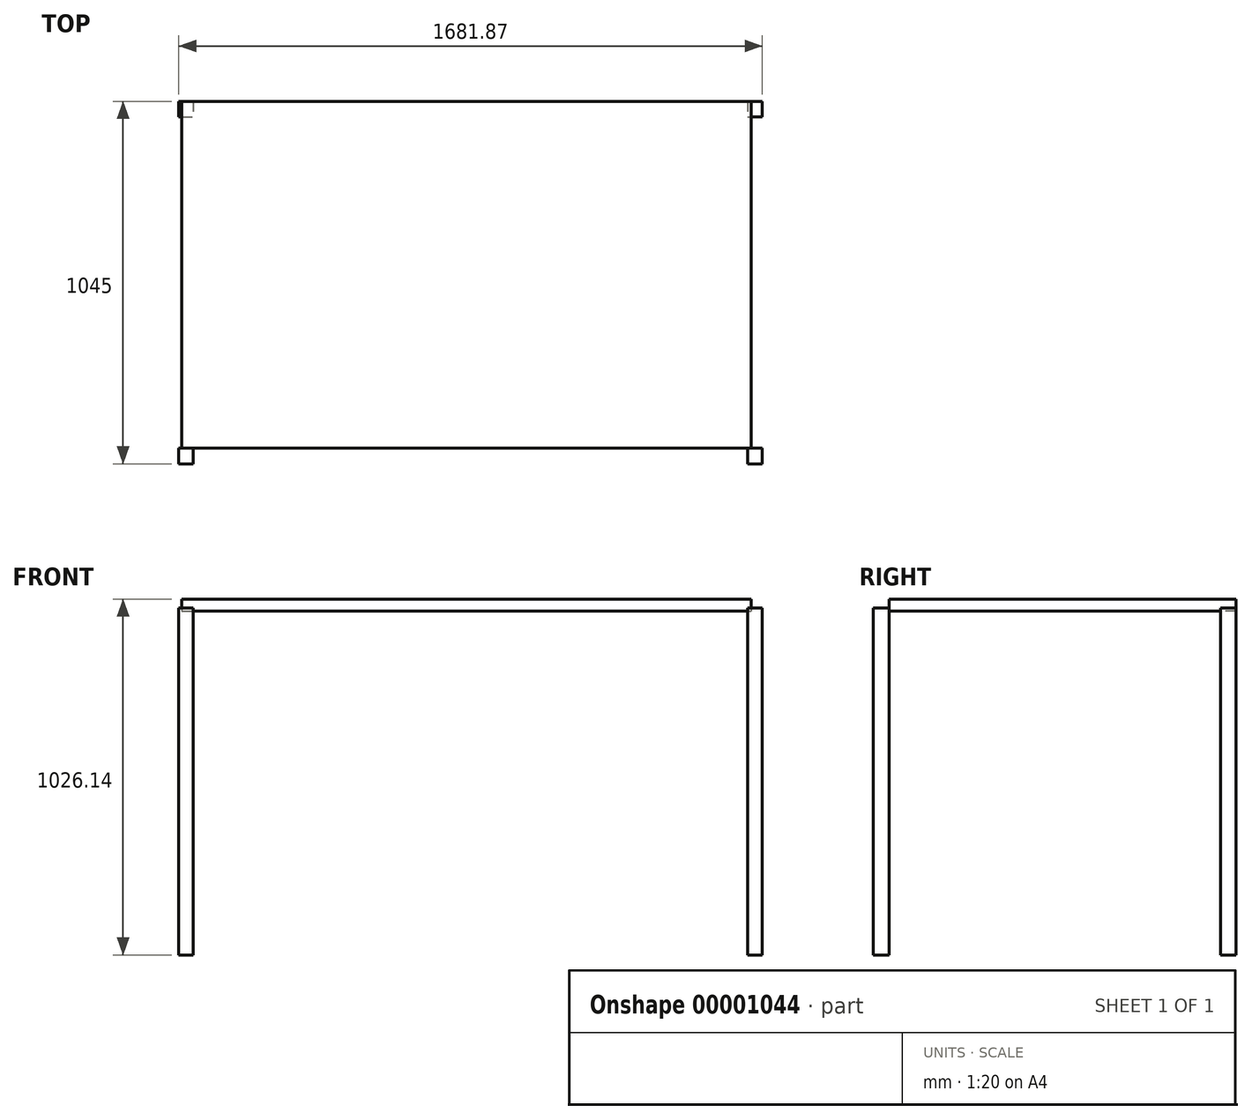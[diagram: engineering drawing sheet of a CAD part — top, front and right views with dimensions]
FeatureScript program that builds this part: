
annotation { "Feature Type Name" : "Feature", "Feature Type Description" : "" }
export const myFeature = defineFeature(function(context is Context, id is Id, definition is map)
    precondition{}
    {
        {
            var Q0;
            Q0=qCreatedBy(makeId("Top.planeOp"),FACE);
            var sketch = newSketch(context, id + "F0", { "sketchPlane" : qUnion([Q0])});
            skLineSegment(sketch, "E0.bottom", {"start": v(-55.77, 808.91) * mm, "end": v(1584.23, 808.91) * mm});
            skLineSegment(sketch, "E0.top", {"start": v(-55.77, -191.09) * mm, "end": v(1584.23, -191.09) * mm});
            skLineSegment(sketch, "E0.left", {"start": v(-55.77, 808.91) * mm, "end": v(-55.77, -191.09) * mm});
            skLineSegment(sketch, "E0.right", {"start": v(1584.23, 808.91) * mm, "end": v(1584.23, -191.09) * mm});
            skSolve(sketch);
        }
        {
            var Q0;
            Q0=qCreatedBy(makeId("Top.planeOp"),FACE);
            var sketch = newSketch(context, id + "F1", { "sketchPlane" : qUnion([Q0])});
            skLineSegment(sketch, "E1.bottom", {"start": v(-344.59, -179) * mm, "end": v(-302.72, -179) * mm});
            skLineSegment(sketch, "E1.top", {"start": v(-344.59, -224) * mm, "end": v(-302.72, -224) * mm});
            skLineSegment(sketch, "E1.left", {"start": v(-344.59, -179) * mm, "end": v(-344.59, -224) * mm});
            skLineSegment(sketch, "E1.right", {"start": v(-302.72, -179) * mm, "end": v(-302.72, -224) * mm});
            skSolve(sketch);
        }
        {
            var Q0;
            Q0=makeQuery(id+"F0.imprint","IMPRINT",FACE,{"disambiguationData":[TD([[makeQuery(id+"F0.imprint","IMPRINT",EDGE,{"derivedFrom":sQuery(id+"F0.wireOp",EDGE,"E0.bottom")}),-1.0]])]});
            extrude(context, id + "F2", {"entities" : qUnion([Q0]), "depth" : 35 * mm});
        }
        {
            var Q0;
            Q0 = qSketchRegion(id + "F1", true);
            extrude(context, id + "F3", {"entities" : qUnion([Q0]), "depth" : 1000 * mm});
        }
        {
            var Q0;
            Q0=makeQuery(id+"F3.opExtrude","SWEPT_BODY",BODY,{"disambiguationData":[OSD([sQuery(id+"F1.wireOp",EDGE,"E1.bottom"),sQuery(id+"F1.wireOp",EDGE,"E1.top"),sQuery(id+"F1.wireOp",EDGE,"E1.left"),sQuery(id+"F1.wireOp",EDGE,"E1.right")])]});
            transform(context, id + "F4", {"entities" : qUnion([Q0]), "transformType" : TransformType.TRANSLATION_3D, "dx" : 0 * mm, "dy" : 1000 * mm, "dz" : 0 * mm, "makeCopy" : true});
        }
        {
            var Q0;
            Q0=makeQuery(id+"F3.opExtrude","SWEPT_BODY",BODY,{"disambiguationData":[OSD([sQuery(id+"F1.wireOp",EDGE,"E1.bottom"),sQuery(id+"F1.wireOp",EDGE,"E1.top"),sQuery(id+"F1.wireOp",EDGE,"E1.left"),sQuery(id+"F1.wireOp",EDGE,"E1.right")])]});
            transform(context, id + "F5", {"entities" : qUnion([Q0]), "transformType" : TransformType.TRANSLATION_3D, "dx" : 1640 * mm, "dy" : 0 * mm, "dz" : 0 * mm, "makeCopy" : true});
        }
        {
            var Q0;
            Q0=makeQuery(id+"F4.opPattern","COPY",BODY,{"derivedFrom":makeQuery(id+"F3.opExtrude","SWEPT_BODY",BODY,{"disambiguationData":[OSD([sQuery(id+"F1.wireOp",EDGE,"E1.bottom"),sQuery(id+"F1.wireOp",EDGE,"E1.top"),sQuery(id+"F1.wireOp",EDGE,"E1.left"),sQuery(id+"F1.wireOp",EDGE,"E1.right")])]}),"instanceName":"1"});
            transform(context, id + "F6", {"entities" : qUnion([Q0]), "transformType" : TransformType.TRANSLATION_3D, "dx" : 1640 * mm, "dy" : 0 * mm, "dz" : 0 * mm, "makeCopy" : true});
        }
        {
            var Q0;
            Q0=makeQuery(id+"F2.opExtrude","SWEPT_BODY",BODY,{"disambiguationData":[OSD([sQuery(id+"F0.wireOp",EDGE,"E0.bottom"),sQuery(id+"F0.wireOp",EDGE,"E0.top"),sQuery(id+"F0.wireOp",EDGE,"E0.left"),sQuery(id+"F0.wireOp",EDGE,"E0.right")])]});
            transform(context, id + "F7", {"entities" : qUnion([Q0]), "transformType" : TransformType.TRANSLATION_3D, "dx" : -279.8 * mm, "dy" : 40.27 * mm, "dz" : 1012.18 * mm, "makeCopy" : false});
        }
        {
            var Q0;
            Q0=makeQuery(id+"F2.opExtrude","SWEPT_BODY",BODY,{"disambiguationData":[OSD([sQuery(id+"F0.wireOp",EDGE,"E0.bottom"),sQuery(id+"F0.wireOp",EDGE,"E0.top"),sQuery(id+"F0.wireOp",EDGE,"E0.left"),sQuery(id+"F0.wireOp",EDGE,"E0.right")])]});
            transform(context, id + "F8", {"entities" : qUnion([Q0]), "transformType" : TransformType.TRANSLATION_3D, "dx" : 0 * mm, "dy" : 0 * mm, "dz" : -21.05 * mm, "makeCopy" : false});
        }
        {
            var Q0;
            Q0=makeQuery(id+"F2.opExtrude","SWEPT_BODY",BODY,{"disambiguationData":[OSD([sQuery(id+"F0.wireOp",EDGE,"E0.bottom"),sQuery(id+"F0.wireOp",EDGE,"E0.top"),sQuery(id+"F0.wireOp",EDGE,"E0.left"),sQuery(id+"F0.wireOp",EDGE,"E0.right")])]});
            transform(context, id + "F9", {"entities" : qUnion([Q0]), "transformType" : TransformType.TRANSLATION_3D, "dx" : 0 * mm, "dy" : -28.4 * mm, "dz" : 0 * mm, "makeCopy" : false});
        }
    });
